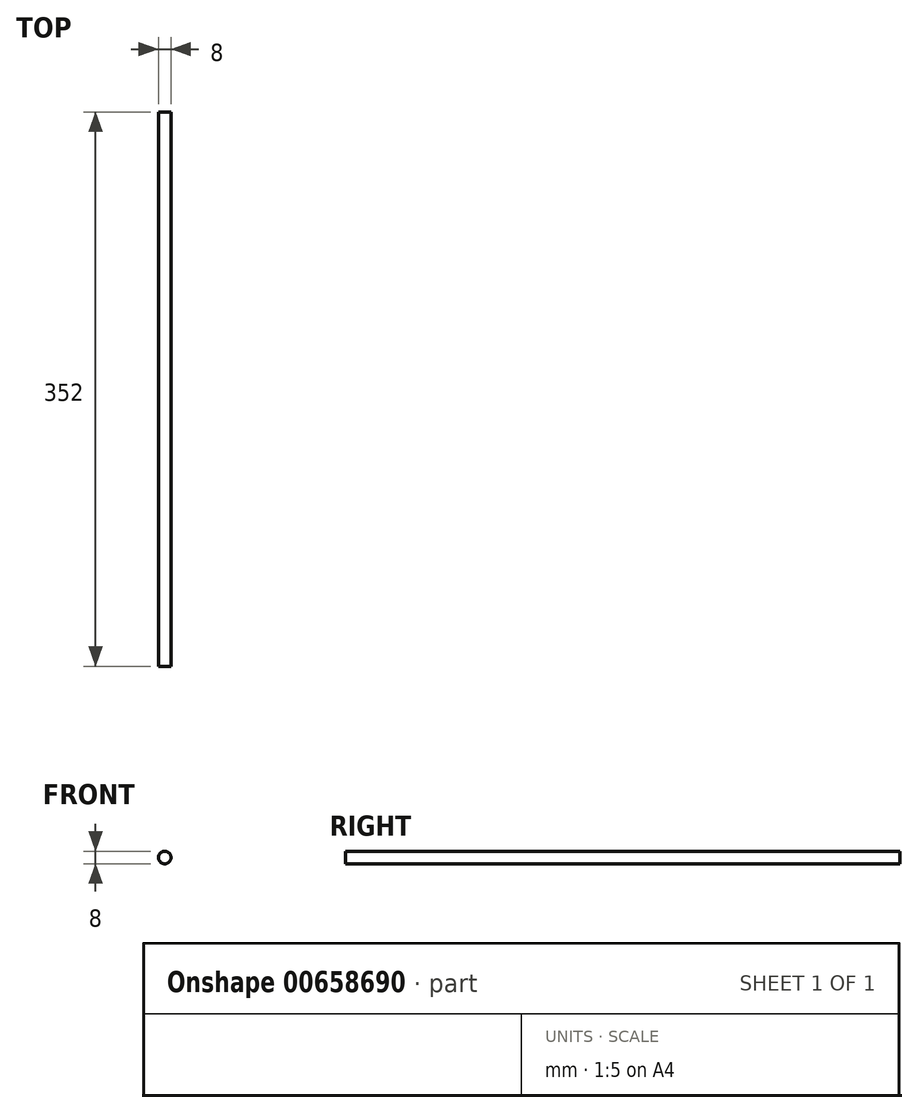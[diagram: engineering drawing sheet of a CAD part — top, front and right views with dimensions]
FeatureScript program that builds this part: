
annotation { "Feature Type Name" : "Feature", "Feature Type Description" : "" }
export const myFeature = defineFeature(function(context is Context, id is Id, definition is map)
    precondition{}
    {
        {
            var Q0;
            Q0=qCreatedBy(makeId("Front.planeOp"),FACE);
            var sketch = newSketch(context, id + "F0", { "sketchPlane" : qUnion([Q0])});
            skCircle(sketch, "E0", {"center": v(0, 0) * mm, "radius": 4 * mm});
            skSolve(sketch);
        }
        {
            var Q0;
            Q0=makeQuery(id+"F0.imprint","IMPRINT",FACE,{"disambiguationData":[TD([[makeQuery(id+"F0.imprint","IMPRINT",EDGE,{"derivedFrom":sQuery(id+"F0.wireOp",EDGE,"E0")}),1.0]])]});
            extrude(context, id + "F1", {"entities" : qUnion([Q0]), "depth" : 352 * mm, "symmetric" : true});
        }
    });
